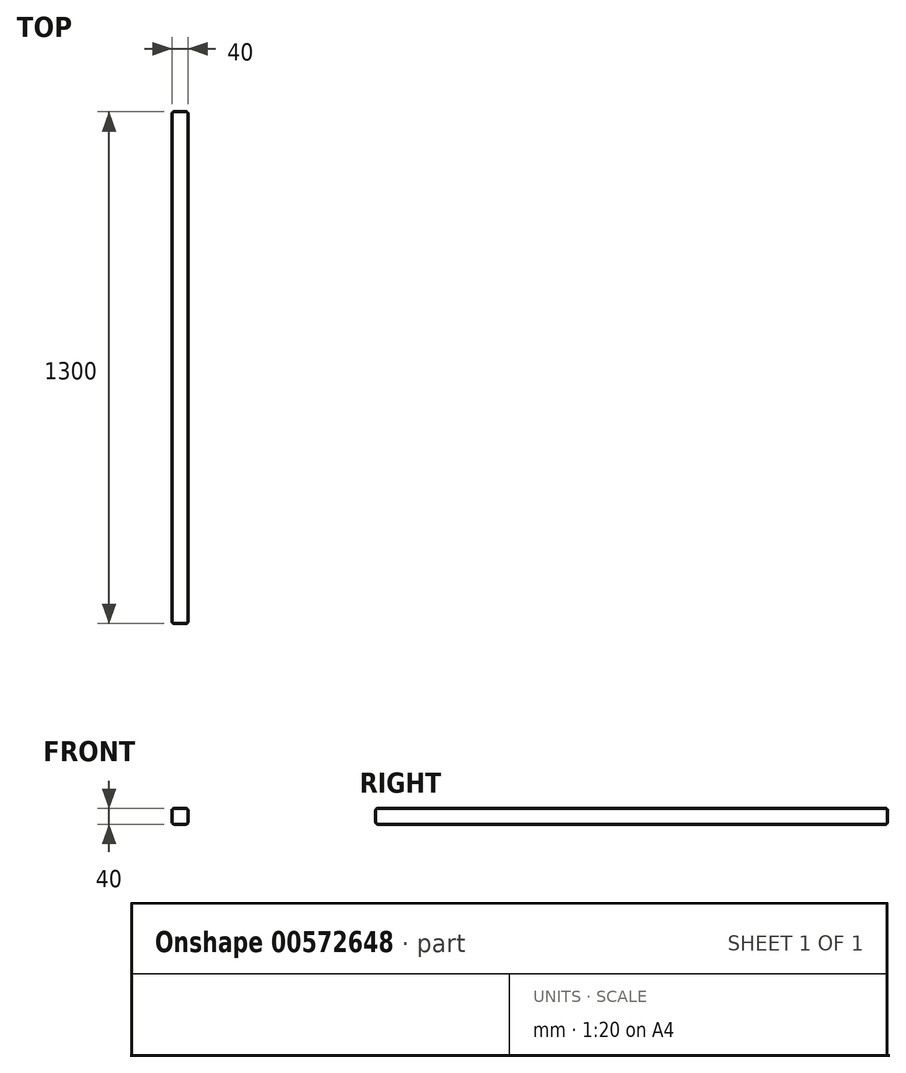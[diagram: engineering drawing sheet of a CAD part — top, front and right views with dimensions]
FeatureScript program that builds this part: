
annotation { "Feature Type Name" : "Feature", "Feature Type Description" : "" }
export const myFeature = defineFeature(function(context is Context, id is Id, definition is map)
    precondition{}
    {
        {
            var Q0;
            Q0=qCreatedBy(makeId("Front.planeOp"),FACE);
            var sketch = newSketch(context, id + "F0", { "sketchPlane" : qUnion([Q0])});
            skLineSegment(sketch, "E0.bottom", {"start": v(-25.8, 26.08) * mm, "end": v(14.2, 26.08) * mm});
            skLineSegment(sketch, "E0.top", {"start": v(-25.8, -13.92) * mm, "end": v(14.2, -13.92) * mm});
            skLineSegment(sketch, "E0.left", {"start": v(-25.8, 26.08) * mm, "end": v(-25.8, -13.92) * mm});
            skLineSegment(sketch, "E0.right", {"start": v(14.2, 26.08) * mm, "end": v(14.2, -13.92) * mm});
            skSolve(sketch);
        }
        {
            var Q0;
            Q0 = qSketchRegion(id + "F0", true);
            extrude(context, id + "F1", {"entities" : qUnion([Q0]), "depth" : 1300 * mm, "offsetDistance" : 25 * mm});
        }
        {
            var Q0;
            Q0=makeQuery(id+"F1.opExtrude","SWEPT_FACE",FACE,{"disambiguationData":[OSD([sQuery(id+"F0.wireOp",EDGE,"E0.bottom")])]});
            var Q1;
            Q1=makeQuery(id+"F1.opExtrude","SWEPT_FACE",FACE,{"disambiguationData":[OSD([sQuery(id+"F0.wireOp",EDGE,"E0.right")])]});
            var Q2;
            Q2=makeQuery(id+"F1.opExtrude","SWEPT_FACE",FACE,{"disambiguationData":[OSD([sQuery(id+"F0.wireOp",EDGE,"E0.left")])]});
            var Q3;
            Q3=makeQuery(id+"F1.opExtrude","SWEPT_FACE",FACE,{"disambiguationData":[OSD([sQuery(id+"F0.wireOp",EDGE,"E0.top")])]});
            fillet(context, id + "F2", {"entities" : qUnion([Q0, Q1, Q2, Q3]), "radius" : 5 * mm, "tangentPropagation" : true, "allowEdgeOverflow" : false});
        }
    });
